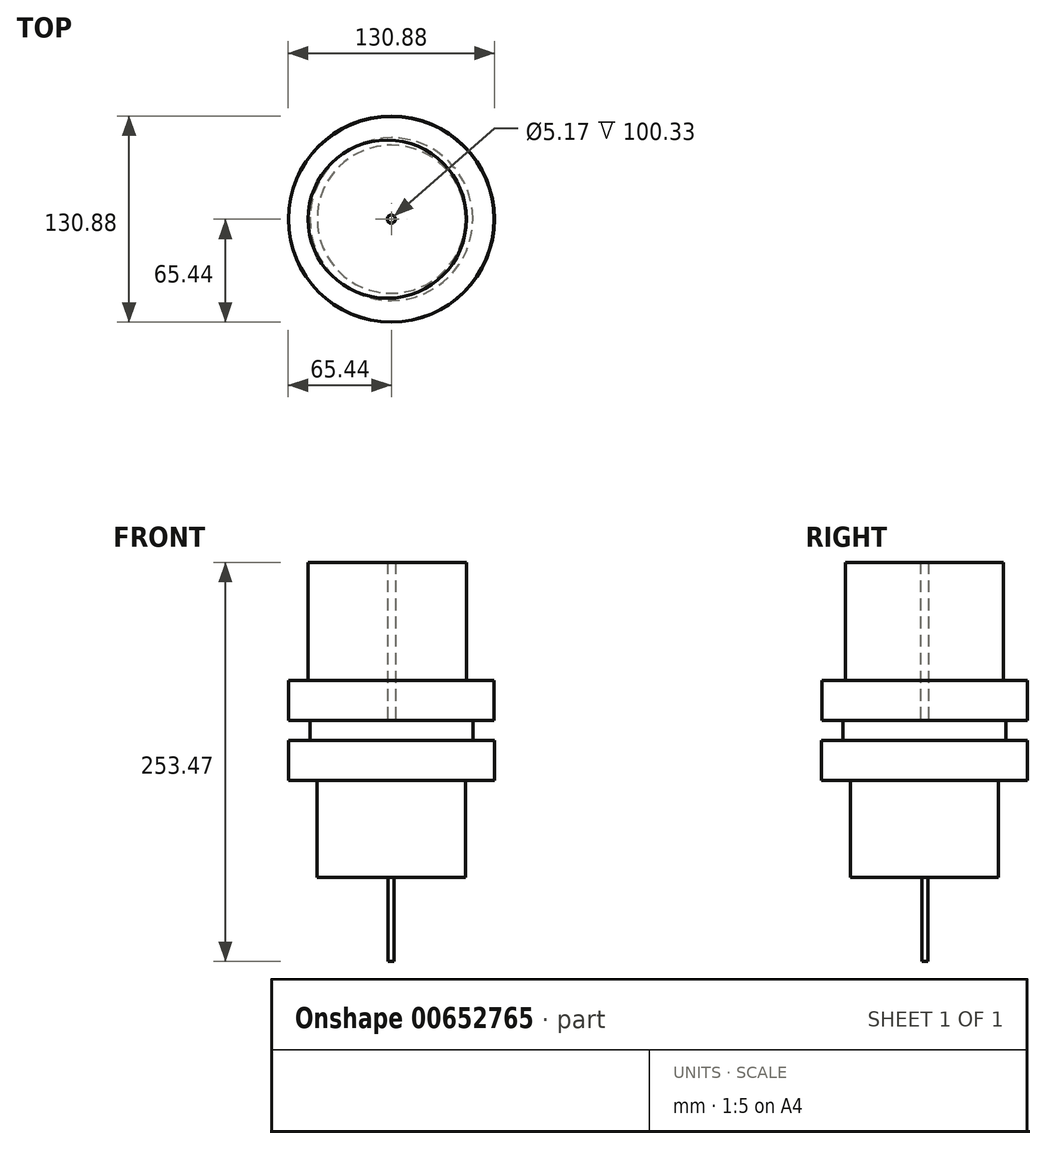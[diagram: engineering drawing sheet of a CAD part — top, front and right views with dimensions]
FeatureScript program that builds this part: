
annotation { "Feature Type Name" : "Feature", "Feature Type Description" : "" }
export const myFeature = defineFeature(function(context is Context, id is Id, definition is map)
    precondition{}
    {
        {
            var Q0;
            Q0=qCreatedBy(makeId("Top.planeOp"),FACE);
            var sketch = newSketch(context, id + "F0", { "sketchPlane" : qUnion([Q0])});
            skCircle(sketch, "E0", {"center": v(0, 0) * mm, "radius": 65.44 * mm});
            skSolve(sketch);
        }
        {
            var Q0;
            Q0=makeQuery(id+"F0.imprint","IMPRINT",FACE,{"disambiguationData":[TD([[makeQuery(id+"F0.imprint","IMPRINT",EDGE,{"derivedFrom":sQuery(id+"F0.wireOp",EDGE,"E0")}),1.0]])]});
            extrude(context, id + "F1", {"entities" : qUnion([Q0]), "depth" : 25.4 * mm, "offsetDistance" : 25.4 * mm});
        }
        {
            var Q0;
            Q0=makeQuery(id+"F1.opExtrude","CAP_FACE",FACE,{"disambiguationData":[OSD([sQuery(id+"F0.wireOp",EDGE,"E0")])],"isStart":false});
            var sketch = newSketch(context, id + "F2", { "sketchPlane" : qUnion([Q0])});
            skCircle(sketch, "E1", {"center": v(0, 0) * mm, "radius": 51.72 * mm});
            skSolve(sketch);
        }
        {
            var Q0;
            Q0=makeQuery(id+"F2.imprint","IMPRINT",FACE,{"disambiguationData":[TD([[makeQuery(id+"F2.imprint","IMPRINT",EDGE,{"derivedFrom":sQuery(id+"F2.wireOp",EDGE,"E1")}),1.0]])]});
            extrude(context, id + "F3", {"entities" : qUnion([Q0]), "operationType" : NewBodyOperationType.ADD, "depth" : 12.93 * mm, "offsetDistance" : 25.4 * mm});
        }
        {
            var Q0;
            Q0=makeQuery(id+"F3.opExtrude","CAP_FACE",FACE,{"disambiguationData":[OSD([sQuery(id+"F2.wireOp",EDGE,"E1")])],"isStart":false});
            var sketch = newSketch(context, id + "F4", { "sketchPlane" : qUnion([Q0])});
            skCircle(sketch, "E2", {"center": v(0, 0) * mm, "radius": 2.59 * mm});
            skCircle(sketch, "E3", {"center": v(0, 0) * mm, "radius": 65.26 * mm});
            skSolve(sketch);
        }
        {
            var Q0;
            Q0=makeQuery(id+"F4.imprint","IMPRINT",FACE,{"disambiguationData":[TD([[makeQuery(id+"F4.imprint","IMPRINT",EDGE,{"derivedFrom":sQuery(id+"F4.wireOp",EDGE,"E2")}),-1.0]])]});
            var Q1;
            Q1 = qSketchRegion(id + "F4", true);
            extrude(context, id + "F5", {"entities" : qUnion([Q0, Q1]), "operationType" : NewBodyOperationType.ADD, "depth" : 25.4 * mm, "offsetDistance" : 25.4 * mm});
        }
        {
            var Q0;
            Q0=makeQuery(id+"F1.opExtrude","CAP_FACE",FACE,{"disambiguationData":[OSD([sQuery(id+"F0.wireOp",EDGE,"E0")])],"isStart":true});
            var sketch = newSketch(context, id + "F6", { "sketchPlane" : qUnion([Q0])});
            skCircle(sketch, "E4", {"center": v(0, 0) * mm, "radius": 47.07 * mm});
            skSolve(sketch);
        }
        {
            var Q0;
            Q0=makeQuery(id+"F6.imprint","IMPRINT",FACE,{"disambiguationData":[TD([[makeQuery(id+"F6.imprint","IMPRINT",EDGE,{"derivedFrom":sQuery(id+"F6.wireOp",EDGE,"E4")}),1.0]])]});
            extrude(context, id + "F7", {"entities" : qUnion([Q0]), "operationType" : NewBodyOperationType.ADD, "depth" : 61.47 * mm, "offsetDistance" : 25.4 * mm});
        }
        {
            var Q0;
            Q0=makeQuery(id+"F5.opExtrude","CAP_FACE",FACE,{"disambiguationData":[OSD([sQuery(id+"F4.wireOp",EDGE,"E2"),sQuery(id+"F4.wireOp",EDGE,"E3")])],"isStart":false});
            var sketch = newSketch(context, id + "F8", { "sketchPlane" : qUnion([Q0])});
            skCircle(sketch, "E5", {"center": v(-2.59, 0) * mm, "radius": 50.23 * mm});
            skSolve(sketch);
        }
        {
            var Q0;
            Q0=makeQuery(id+"F8.imprint","IMPRINT",FACE,{"disambiguationData":[TD([[makeQuery(id+"F8.imprint","IMPRINT",EDGE,{"derivedFrom":sQuery(id+"F8.wireOp",EDGE,"E5")}),1.0]])]});
            extrude(context, id + "F9", {"entities" : qUnion([Q0]), "operationType" : NewBodyOperationType.ADD, "depth" : 74.93 * mm, "offsetDistance" : 25.4 * mm});
        }
        {
            var Q0;
            Q0=makeQuery(id+"F7.opExtrude","CAP_FACE",FACE,{"disambiguationData":[OSD([sQuery(id+"F6.wireOp",EDGE,"E4")])],"isStart":false});
            var sketch = newSketch(context, id + "F10", { "sketchPlane" : qUnion([Q0])});
            skSolve(sketch);
        }
        {
            var Q0;
            Q0=makeQuery(id+"F10.imprint","IMPRINT",FACE,{"disambiguationData":[TD([[makeQuery(id+"F10.imprint","IMPRINT",EDGE,{"derivedFrom":makeQuery(id+"F7.opExtrude","CAP_EDGE",EDGE,{"disambiguationData":[OSD([sQuery(id+"F6.wireOp",EDGE,"E4")])],"isStart":false})}),1.0]])]});
            var sketch = newSketch(context, id + "F11", { "sketchPlane" : qUnion([Q0])});
            skLineSegment(sketch, "E6.bottom", {"start": v(4.73, -6.53) * mm, "end": v(-4.5, -6.53) * mm});
            skLineSegment(sketch, "E6.top", {"start": v(4.73, 5.35) * mm, "end": v(-4.5, 5.35) * mm});
            skLineSegment(sketch, "E6.left", {"start": v(4.73, -6.53) * mm, "end": v(4.73, 5.35) * mm});
            skLineSegment(sketch, "E6.right", {"start": v(-4.5, -6.53) * mm, "end": v(-4.5, 5.35) * mm});
            skSolve(sketch);
        }
        {
            var Q0;
            Q0=makeQuery(id+"F11.imprint","IMPRINT",FACE,{"disambiguationData":[TD([[makeQuery(id+"F11.imprint","IMPRINT",EDGE,{"derivedFrom":sQuery(id+"F11.wireOp",EDGE,"E6.bottom")}),-1.0]])]});
            var Q1;
            Q1=makeQuery(id+"F10.imprint","IMPRINT",FACE,{"disambiguationData":[TD([[makeQuery(id+"F10.imprint","IMPRINT",EDGE,{"derivedFrom":makeQuery(id+"F7.opExtrude","CAP_EDGE",EDGE,{"disambiguationData":[OSD([sQuery(id+"F6.wireOp",EDGE,"E4")])],"isStart":false})}),1.0]])]});
            extrude(context, id + "F12", {"entities" : qUnion([Q0, Q1]), "operationType" : NewBodyOperationType.ADD, "oppositeDirection" : true, "depth" : 1.52 * mm, "offsetDistance" : 25.4 * mm});
        }
        {
            var Q0;
            Q0=makeQuery(id+"F7.opExtrude","CAP_FACE",FACE,{"disambiguationData":[OSD([sQuery(id+"F6.wireOp",EDGE,"E4")])],"isStart":false});
            var sketch = newSketch(context, id + "F13", { "sketchPlane" : qUnion([Q0])});
            skLineSegment(sketch, "E7.bottom", {"start": v(1.7, -2.24) * mm, "end": v(-2.2, -2.24) * mm});
            skLineSegment(sketch, "E7.top", {"start": v(1.7, 1.72) * mm, "end": v(-2.2, 1.72) * mm});
            skLineSegment(sketch, "E7.left", {"start": v(1.7, -2.24) * mm, "end": v(1.7, 1.72) * mm});
            skLineSegment(sketch, "E7.right", {"start": v(-2.2, -2.24) * mm, "end": v(-2.2, 1.72) * mm});
            skSolve(sketch);
        }
        {
            var Q0;
            Q0=makeQuery(id+"F13.imprint","IMPRINT",FACE,{"disambiguationData":[TD([[makeQuery(id+"F13.imprint","IMPRINT",EDGE,{"derivedFrom":sQuery(id+"F13.wireOp",EDGE,"E7.bottom")}),-1.0]])]});
            extrude(context, id + "F14", {"entities" : qUnion([Q0]), "operationType" : NewBodyOperationType.ADD, "depth" : 53.34 * mm, "offsetDistance" : 25.4 * mm});
        }
    });
